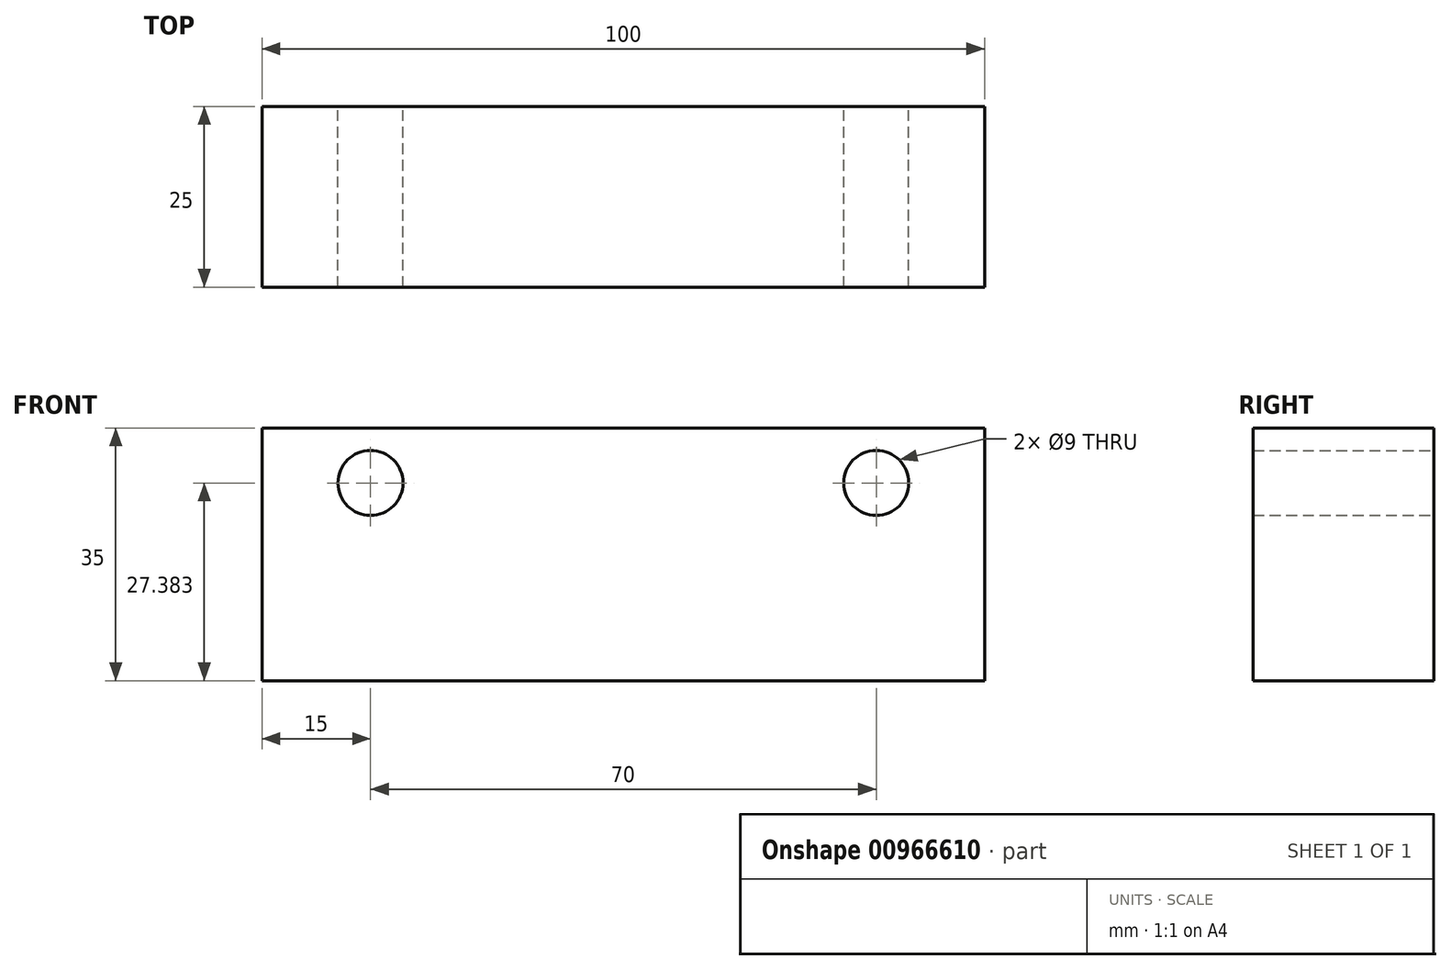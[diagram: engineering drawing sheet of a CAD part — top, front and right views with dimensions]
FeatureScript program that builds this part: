
annotation { "Feature Type Name" : "Feature", "Feature Type Description" : "" }
export const myFeature = defineFeature(function(context is Context, id is Id, definition is map)
    precondition{}
    {
        {
            var Q0;
            Q0=qCreatedBy(makeId("Front.planeOp"),FACE);
            var sketch = newSketch(context, id + "F0", { "sketchPlane" : qUnion([Q0])});
            skLineSegment(sketch, "E0.bottom", {"start": v(50, 17.5) * mm, "end": v(-50, 17.5) * mm});
            skLineSegment(sketch, "E0.top", {"start": v(50, -17.5) * mm, "end": v(-50, -17.5) * mm});
            skLineSegment(sketch, "E0.left", {"start": v(50, 17.5) * mm, "end": v(50, -17.5) * mm});
            skLineSegment(sketch, "E0.right", {"start": v(-50, 17.5) * mm, "end": v(-50, -17.5) * mm});
            skPoint(sketch, "E0.middle", {"position": v(0, 0) * mm});
            skCircle(sketch, "E1", {"center": v(-35, 9.88) * mm, "radius": 4.5 * mm});
            skCircle(sketch, "E2.MirrorC", {"center": v(35, 9.88) * mm, "radius": 4.5 * mm});
            skSolve(sketch);
        }
        {
            var Q0;
            Q0 = qSketchRegion(id + "F0", true);
            var Q1;
            Q1=makeQuery(id+"F0.imprint","IMPRINT",FACE,{"disambiguationData":[TD([[makeQuery(id+"F0.imprint","IMPRINT",EDGE,{"derivedFrom":sQuery(id+"F0.wireOp",EDGE,"E0.bottom")}),1.0]])]});
            extrude(context, id + "F1", {"entities" : qUnion([Q0, Q1]), "depth" : 25 * mm, "offsetDistance" : 25 * mm});
        }
    });
